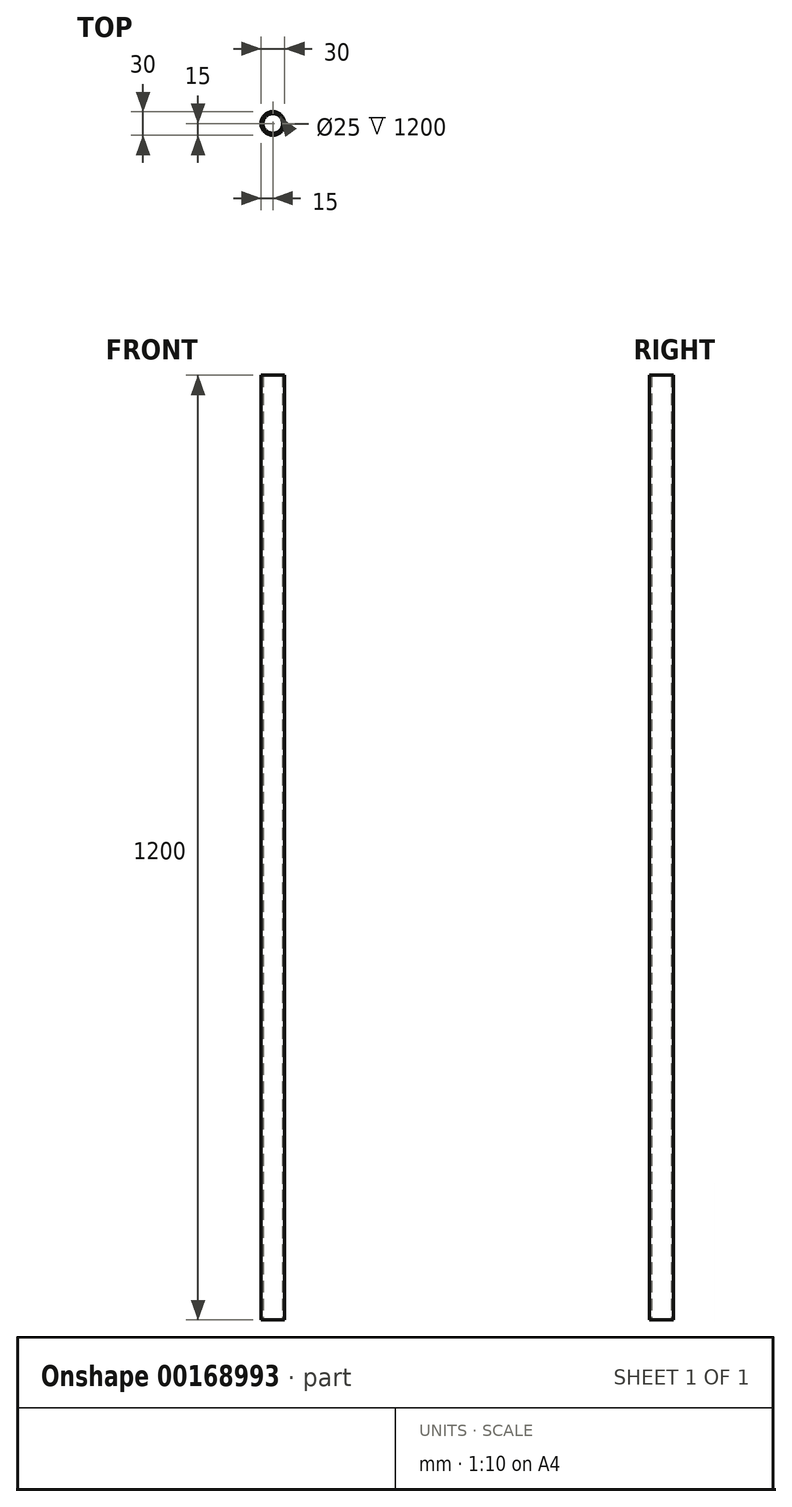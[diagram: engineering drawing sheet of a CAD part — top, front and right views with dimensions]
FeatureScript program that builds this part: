
annotation { "Feature Type Name" : "Feature", "Feature Type Description" : "" }
export const myFeature = defineFeature(function(context is Context, id is Id, definition is map)
    precondition{}
    {
        {
            var Q0;
            Q0=qCreatedBy(makeId("Top.planeOp"),FACE);
            var sketch = newSketch(context, id + "F0", { "sketchPlane" : qUnion([Q0])});
            skCircle(sketch, "E0", {"center": v(0, 0) * mm, "radius": 12.5 * mm});
            skCircle(sketch, "E1", {"center": v(0, 0) * mm, "radius": 15 * mm});
            skSolve(sketch);
        }
        {
            var Q0;
            Q0=makeQuery(id+"F0.imprint","IMPRINT",FACE,{"disambiguationData":[TD([[makeQuery(id+"F0.imprint","IMPRINT",EDGE,{"derivedFrom":sQuery(id+"F0.wireOp",EDGE,"E0")}),-1.0]])]});
            extrude(context, id + "F1", {"entities" : qUnion([Q0]), "depth" : 1200 * mm});
        }
    });
